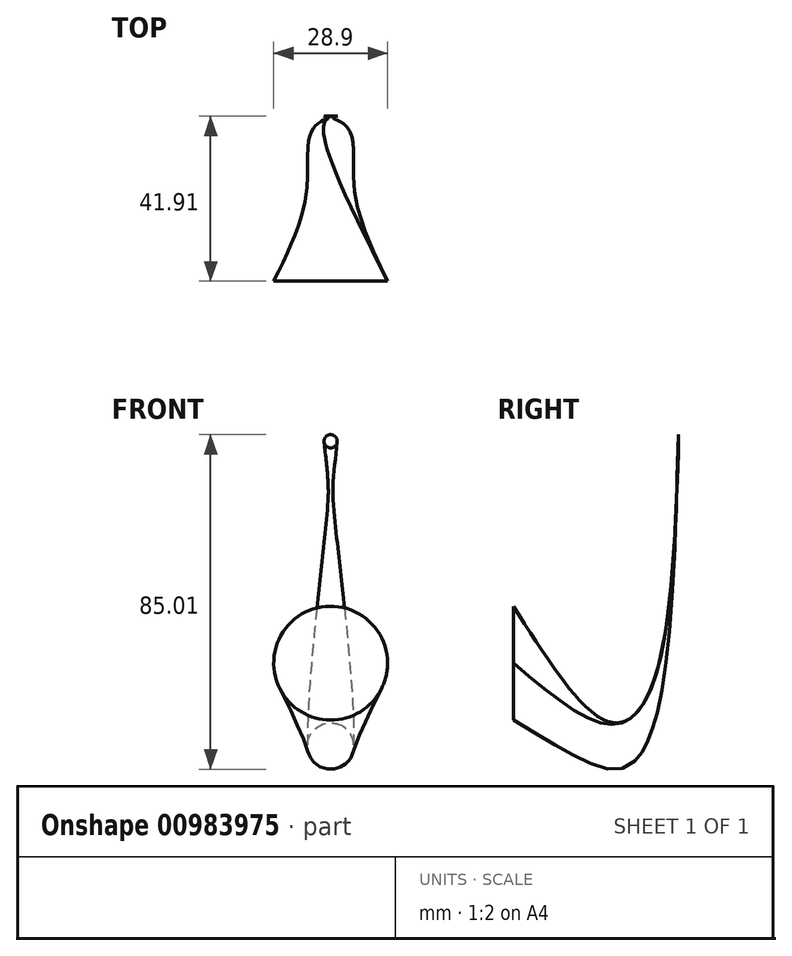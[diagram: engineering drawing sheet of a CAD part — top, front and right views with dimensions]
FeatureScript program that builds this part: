
annotation { "Feature Type Name" : "Feature", "Feature Type Description" : "" }
export const myFeature = defineFeature(function(context is Context, id is Id, definition is map)
    precondition{}
    {
        {
            var Q0;
            Q0=qCreatedBy(makeId("Front.planeOp"),FACE);
            var sketch = newSketch(context, id + "F0", { "sketchPlane" : qUnion([Q0])});
            skCircle(sketch, "E0", {"center": v(0, -45.42) * mm, "radius": 14.45 * mm});
            skSolve(sketch);
        }
        {
            var Q0;
            Q0=qCreatedBy(makeId("Front.planeOp"),FACE);
            cPlane(context, id + "F1", {"entities" : qUnion([Q0]), "cplaneType" : CPlaneType.OFFSET, "offset" : 22.35 * mm, "oppositeDirection" : true, "width" : 152.4 * mm, "height" : 152.4 * mm});
        }
        {
            var Q0;
            Q0=qCreatedBy(id+"F1.planeOp",FACE);
            var sketch = newSketch(context, id + "F2", { "sketchPlane" : qUnion([Q0])});
            skCircle(sketch, "E1", {"center": v(0, -65.72) * mm, "radius": 6.17 * mm});
            skSolve(sketch);
        }
        {
            var Q0;
            Q0=qCreatedBy(makeId("Front.planeOp"),FACE);
            cPlane(context, id + "F3", {"entities" : qUnion([Q0]), "cplaneType" : CPlaneType.OFFSET, "offset" : 41.9 * mm, "oppositeDirection" : true, "width" : 152.4 * mm, "height" : 152.4 * mm});
        }
        {
            var Q0;
            Q0=qCreatedBy(id+"F3.planeOp",FACE);
            var sketch = newSketch(context, id + "F4", { "sketchPlane" : qUnion([Q0])});
            skCircle(sketch, "E2", {"center": v(0, 10.94) * mm, "radius": 1.68 * mm});
            skSolve(sketch);
        }
        {
            var Q0;
            Q0=sQuery(id+"F0.wireOp",EDGE,"E0");
            var Q1;
            Q1=sQuery(id+"F2.wireOp",EDGE,"E1");
            var Q2;
            Q2=sQuery(id+"F4.wireOp",EDGE,"E2");
            loft(context, id + "F5", {"bodyType" : ToolBodyType.SURFACE, "wireProfilesArray" : [{ "wireProfileEntities" : qUnion([Q0]) }, { "wireProfileEntities" : qUnion([Q1]) }, { "wireProfileEntities" : qUnion([Q2]) }]});
        }
    });
